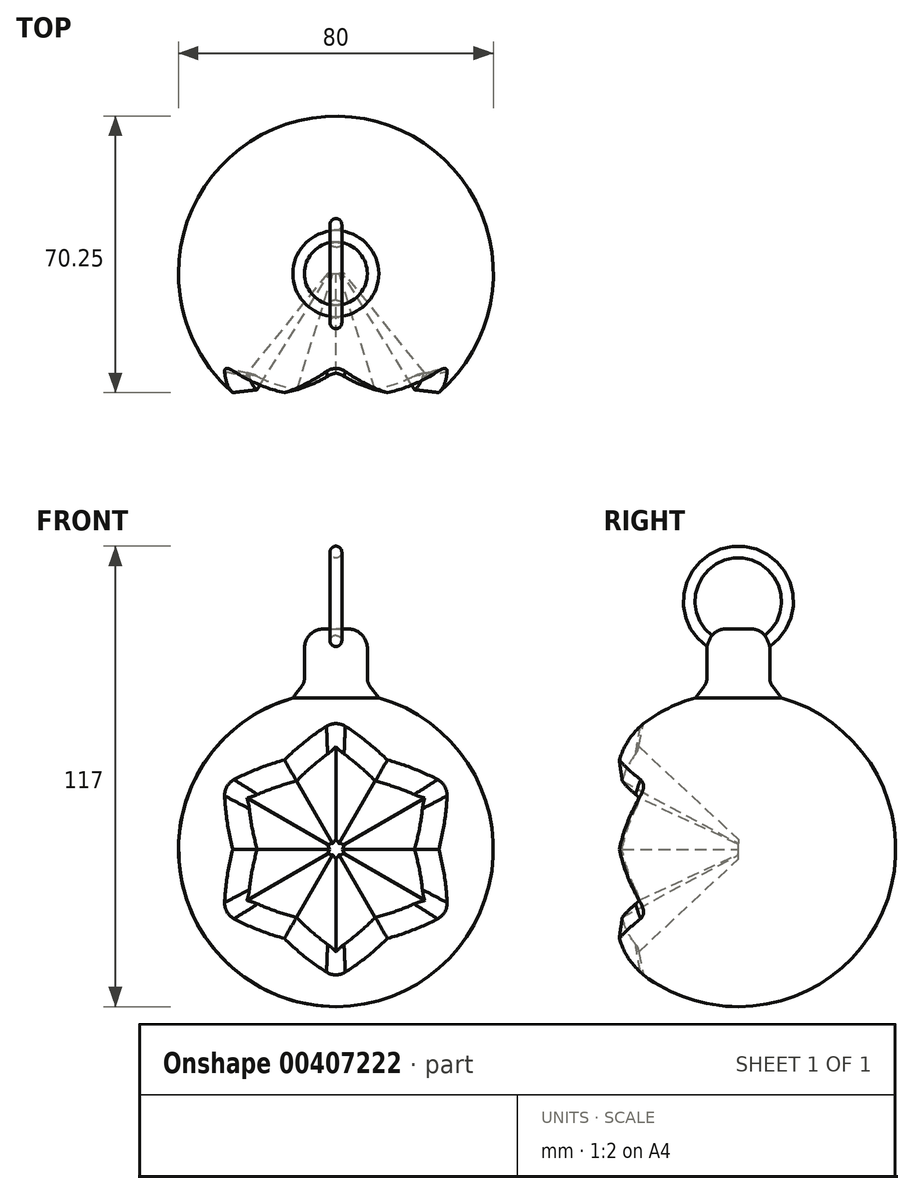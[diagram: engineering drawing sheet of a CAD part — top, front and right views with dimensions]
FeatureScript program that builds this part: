
annotation { "Feature Type Name" : "Feature", "Feature Type Description" : "" }
export const myFeature = defineFeature(function(context is Context, id is Id, definition is map)
    precondition{}
    {
        {
            var Q0;
            Q0=qCreatedBy(makeId("Front.planeOp"),FACE);
            var sketch = newSketch(context, id + "F0", { "sketchPlane" : qUnion([Q0])});
            skLineSegment(sketch, "E0", {"start": v(0, 40) * mm, "end": v(0, -40) * mm});
            skArc(sketch, "E1", {"start": v(0, 40) * mm, "mid": v(40, 0) * mm, "end": v(0, -40) * mm});
            skSolve(sketch);
        }
        {
            var Q0;
            Q0 = qSketchRegion(id + "F0", true);
            var Q1;
            Q1=sQuery(id+"F0.wireOp",EDGE,"E0");
            revolve(context, id + "F1", {"entities" : qUnion([Q0]), "axis" : qUnion([Q1]), "revolveType" : RevolveType.FULL});
        }
        {
            var Q0;
            Q0=qCreatedBy(makeId("Top.planeOp"),FACE);
            var sketch = newSketch(context, id + "F2", { "sketchPlane" : qUnion([Q0])});
            skCircle(sketch, "E2", {"center": v(0, 0) * mm, "radius": 8 * mm});
            skSolve(sketch);
        }
        {
            var Q0;
            Q0 = qSketchRegion(id + "F2", true);
            var Q1;
            Q1=sQuery(id+"F2.wireOp",EDGE,"E2");
            extrude(context, id + "F3", {"entities" : qUnion([Q0]), "operationType" : NewBodyOperationType.ADD, "surfaceEntities" : qUnion([Q1]), "depth" : 56 * mm});
        }
        {
            var Q0;
            Q0=qCreatedBy(makeId("Right.planeOp"),FACE);
            var sketch = newSketch(context, id + "F4", { "sketchPlane" : qUnion([Q0])});
            skCircle(sketch, "E3", {"center": v(0, 63) * mm, "radius": 11 * mm});
            skCircle(sketch, "E4.0", {"center": v(0, 63) * mm, "radius": 14 * mm});
            skSolve(sketch);
        }
        {
            var Q0;
            Q0 = qSketchRegion(id + "F4", true);
            extrude(context, id + "F5", {"entities" : qUnion([Q0]), "operationType" : NewBodyOperationType.ADD, "endBound" : BoundingType.SYMMETRIC, "depth" : 3 * mm});
        }
        {
            var Q0;
            Q0=makeQuery(id+"F5.opExtrude","CAP_EDGE",EDGE,{"disambiguationData":[OSD([sQuery(id+"F4.wireOp",EDGE,"E3")])],"isStart":true});
            var Q1;
            Q1=makeQuery(id+"F5.opExtrude","CAP_EDGE",EDGE,{"disambiguationData":[OSD([sQuery(id+"F4.wireOp",EDGE,"E4.0")])],"isStart":true});
            var Q2;
            Q2=makeQuery(id+"F5.opExtrude","CAP_EDGE",EDGE,{"disambiguationData":[OSD([sQuery(id+"F4.wireOp",EDGE,"E3")])],"isStart":false});
            var Q3;
            Q3=makeQuery(id+"F5.opExtrude","CAP_EDGE",EDGE,{"disambiguationData":[OSD([sQuery(id+"F4.wireOp",EDGE,"E4.0")])],"isStart":false});
            fillet(context, id + "F6", {"entities" : qUnion([Q0, Q1, Q2, Q3]), "radius" : 1.5 * mm, "tangentPropagation" : true, "allowEdgeOverflow" : false});
        }
        {
            var Q0;
            Q0=makeQuery(id+"F3.opExtrude","CAP_EDGE",EDGE,{"disambiguationData":[OSD([sQuery(id+"F2.wireOp",EDGE,"E2")])],"isStart":false});
            fillet(context, id + "F7", {"entities" : qUnion([Q0]), "radius" : 5 * mm, "tangentPropagation" : true, "allowEdgeOverflow" : false});
        }
        {
            var Q0;
            Q0=makeQuery(id+"F3.boolean.opBoolean","INTERSECT",EDGE,{"derivedFrom":[makeQuery(id+"F1.opRevolve","SWEPT_FACE",FACE,{"disambiguationData":[OSD([sQuery(id+"F0.wireOp",EDGE,"E1")])]}),makeQuery(id+"F3.opExtrude","SWEPT_FACE",FACE,{"disambiguationData":[OSD([sQuery(id+"F2.wireOp",EDGE,"E2")])]})]});
            chamfer(context, id + "F8", {"entities" : qUnion([Q0]), "width" : 4 * mm, "tangentPropagation" : true});
        }
        {
            var Q0;
            {var subQ0=makeQuery(id+"F3.opExtrude","SWEPT_FACE",FACE,{"disambiguationData":[OSD([sQuery(id+"F2.wireOp",EDGE,"E2")])]});Q0=makeQuery(id+"F8.opChamfer","BLEND_EDGE",EDGE,{"blendedFrom":[makeQuery(id+"F3.boolean.opBoolean","INTERSECT",EDGE,{"derivedFrom":[makeQuery(id+"F1.opRevolve","SWEPT_FACE",FACE,{"disambiguationData":[OSD([sQuery(id+"F0.wireOp",EDGE,"E1")])]}),subQ0]}),subQ0],"blendedInto":[subQ0]});}
            fillet(context, id + "F9", {"entities" : qUnion([Q0]), "radius" : 3 * mm, "tangentPropagation" : true, "allowEdgeOverflow" : false});
        }
        {
            var Q0;
            Q0=qCreatedBy(makeId("Front.planeOp"),FACE);
            var sketch = newSketch(context, id + "F10", { "sketchPlane" : qUnion([Q0])});
            skCircle(sketch, "E5.cCircle", {"center": v(0, 0) * mm, "radius": 2.5 * mm, "construction": true});
            skLineSegment(sketch, "E5.0", {"start": v(-2.17, 1.25) * mm, "end": v(0, 2.5) * mm, "construction": true});
            skLineSegment(sketch, "E5.1", {"start": v(0, 2.5) * mm, "end": v(2.17, 1.25) * mm, "construction": true});
            skLineSegment(sketch, "E5.2", {"start": v(2.17, 1.25) * mm, "end": v(2.17, -1.25) * mm, "construction": true});
            skLineSegment(sketch, "E5.3", {"start": v(2.17, -1.25) * mm, "end": v(0, -2.5) * mm, "construction": true});
            skLineSegment(sketch, "E5.4", {"start": v(0, -2.5) * mm, "end": v(-2.17, -1.25) * mm, "construction": true});
            skLineSegment(sketch, "E5.5", {"start": v(-2.17, -1.25) * mm, "end": v(-2.17, 1.25) * mm, "construction": true});
            skLineSegment(sketch, "E6", {"start": v(0, 2.5) * mm, "end": v(-0.83, 1.44) * mm});
            skLineSegment(sketch, "E7", {"start": v(-2.17, 1.25) * mm, "end": v(-0.83, 1.44) * mm});
            skLineSegment(sketch, "E8", {"start": v(-2.17, 1.25) * mm, "end": v(-1.67, 0) * mm});
            skLineSegment(sketch, "E9", {"start": v(-1.67, 0) * mm, "end": v(-2.17, -1.25) * mm});
            skLineSegment(sketch, "E10", {"start": v(-2.17, -1.25) * mm, "end": v(-0.83, -1.44) * mm});
            skLineSegment(sketch, "E11", {"start": v(-0.83, -1.44) * mm, "end": v(0, -2.5) * mm});
            skLineSegment(sketch, "E12", {"start": v(0, -2.5) * mm, "end": v(0.83, -1.44) * mm});
            skLineSegment(sketch, "E13", {"start": v(0.83, -1.44) * mm, "end": v(2.17, -1.25) * mm});
            skLineSegment(sketch, "E14", {"start": v(2.17, -1.25) * mm, "end": v(1.67, 0) * mm});
            skLineSegment(sketch, "E15", {"start": v(1.67, 0) * mm, "end": v(2.17, 1.25) * mm});
            skLineSegment(sketch, "E16", {"start": v(2.17, 1.25) * mm, "end": v(0.83, 1.44) * mm});
            skLineSegment(sketch, "E17", {"start": v(0.83, 1.44) * mm, "end": v(0, 2.5) * mm});
            skSolve(sketch);
        }
        {
            var Q0;
            Q0 = qSketchRegion(id + "F10", true);
            extrude(context, id + "F11", {"entities" : qUnion([Q0]), "operationType" : NewBodyOperationType.REMOVE, "depth" : 50 * mm, "hasDraft" : true, "draftAngle" : 30 * degree});
        }
        {
            var Q0;
            Q0=makeQuery(id+"F11.boolean.opBoolean","INTERSECT",EDGE,{"derivedFrom":[makeQuery(id+"F1.opRevolve","SWEPT_FACE",FACE,{"disambiguationData":[OSD([sQuery(id+"F0.wireOp",EDGE,"E1")])]}),makeQuery(id+"F11.opExtrude","SWEPT_FACE",FACE,{"disambiguationData":[OSD([sQuery(id+"F10.wireOp",EDGE,"E17")])]})]});
            var Q1;
            Q1=makeQuery(id+"F11.boolean.opBoolean","INTERSECT",EDGE,{"derivedFrom":[makeQuery(id+"F1.opRevolve","SWEPT_FACE",FACE,{"disambiguationData":[OSD([sQuery(id+"F0.wireOp",EDGE,"E1")])]}),makeQuery(id+"F11.opExtrude","SWEPT_FACE",FACE,{"disambiguationData":[OSD([sQuery(id+"F10.wireOp",EDGE,"E6")])]})]});
            var Q2;
            Q2=makeQuery(id+"F11.boolean.opBoolean","INTERSECT",EDGE,{"derivedFrom":[makeQuery(id+"F1.opRevolve","SWEPT_FACE",FACE,{"disambiguationData":[OSD([sQuery(id+"F0.wireOp",EDGE,"E1")])]}),makeQuery(id+"F11.opExtrude","SWEPT_FACE",FACE,{"disambiguationData":[OSD([sQuery(id+"F10.wireOp",EDGE,"E7")])]})]});
            var Q3;
            Q3=makeQuery(id+"F11.boolean.opBoolean","INTERSECT",EDGE,{"derivedFrom":[makeQuery(id+"F1.opRevolve","SWEPT_FACE",FACE,{"disambiguationData":[OSD([sQuery(id+"F0.wireOp",EDGE,"E1")])]}),makeQuery(id+"F11.opExtrude","SWEPT_FACE",FACE,{"disambiguationData":[OSD([sQuery(id+"F10.wireOp",EDGE,"E8")])]})]});
            var Q4;
            Q4=makeQuery(id+"F11.boolean.opBoolean","INTERSECT",EDGE,{"derivedFrom":[makeQuery(id+"F1.opRevolve","SWEPT_FACE",FACE,{"disambiguationData":[OSD([sQuery(id+"F0.wireOp",EDGE,"E1")])]}),makeQuery(id+"F11.opExtrude","SWEPT_FACE",FACE,{"disambiguationData":[OSD([sQuery(id+"F10.wireOp",EDGE,"E9")])]})]});
            var Q5;
            Q5=makeQuery(id+"F11.boolean.opBoolean","INTERSECT",EDGE,{"derivedFrom":[makeQuery(id+"F1.opRevolve","SWEPT_FACE",FACE,{"disambiguationData":[OSD([sQuery(id+"F0.wireOp",EDGE,"E1")])]}),makeQuery(id+"F11.opExtrude","SWEPT_FACE",FACE,{"disambiguationData":[OSD([sQuery(id+"F10.wireOp",EDGE,"E10")])]})]});
            var Q6;
            Q6=makeQuery(id+"F11.boolean.opBoolean","INTERSECT",EDGE,{"derivedFrom":[makeQuery(id+"F1.opRevolve","SWEPT_FACE",FACE,{"disambiguationData":[OSD([sQuery(id+"F0.wireOp",EDGE,"E1")])]}),makeQuery(id+"F11.opExtrude","SWEPT_FACE",FACE,{"disambiguationData":[OSD([sQuery(id+"F10.wireOp",EDGE,"E11")])]})]});
            var Q7;
            Q7=makeQuery(id+"F11.boolean.opBoolean","INTERSECT",EDGE,{"derivedFrom":[makeQuery(id+"F1.opRevolve","SWEPT_FACE",FACE,{"disambiguationData":[OSD([sQuery(id+"F0.wireOp",EDGE,"E1")])]}),makeQuery(id+"F11.opExtrude","SWEPT_FACE",FACE,{"disambiguationData":[OSD([sQuery(id+"F10.wireOp",EDGE,"E12")])]})]});
            var Q8;
            Q8=makeQuery(id+"F11.boolean.opBoolean","INTERSECT",EDGE,{"derivedFrom":[makeQuery(id+"F1.opRevolve","SWEPT_FACE",FACE,{"disambiguationData":[OSD([sQuery(id+"F0.wireOp",EDGE,"E1")])]}),makeQuery(id+"F11.opExtrude","SWEPT_FACE",FACE,{"disambiguationData":[OSD([sQuery(id+"F10.wireOp",EDGE,"E13")])]})]});
            var Q9;
            Q9=makeQuery(id+"F11.boolean.opBoolean","INTERSECT",EDGE,{"derivedFrom":[makeQuery(id+"F1.opRevolve","SWEPT_FACE",FACE,{"disambiguationData":[OSD([sQuery(id+"F0.wireOp",EDGE,"E1")])]}),makeQuery(id+"F11.opExtrude","SWEPT_FACE",FACE,{"disambiguationData":[OSD([sQuery(id+"F10.wireOp",EDGE,"E14")])]})]});
            var Q10;
            Q10=makeQuery(id+"F11.boolean.opBoolean","INTERSECT",EDGE,{"derivedFrom":[makeQuery(id+"F1.opRevolve","SWEPT_FACE",FACE,{"disambiguationData":[OSD([sQuery(id+"F0.wireOp",EDGE,"E1")])]}),makeQuery(id+"F11.opExtrude","SWEPT_FACE",FACE,{"disambiguationData":[OSD([sQuery(id+"F10.wireOp",EDGE,"E15")])]})]});
            var Q11;
            Q11=makeQuery(id+"F11.boolean.opBoolean","INTERSECT",EDGE,{"derivedFrom":[makeQuery(id+"F1.opRevolve","SWEPT_FACE",FACE,{"disambiguationData":[OSD([sQuery(id+"F0.wireOp",EDGE,"E1")])]}),makeQuery(id+"F11.opExtrude","SWEPT_FACE",FACE,{"disambiguationData":[OSD([sQuery(id+"F10.wireOp",EDGE,"E16")])]})]});
            chamfer(context, id + "F12", {"entities" : qUnion([Q0, Q1, Q2, Q3, Q4, Q5, Q6, Q7, Q8, Q9, Q10, Q11]), "width" : 4 * mm, "tangentPropagation" : true});
        }
        {
            var Q0;
            {var subQ0=makeQuery(id+"F1.opRevolve","SWEPT_FACE",FACE,{"disambiguationData":[OSD([sQuery(id+"F0.wireOp",EDGE,"E1")])]});Q0=makeQuery(id+"F12.opChamfer","BLEND_EDGE",EDGE,{"blendedFrom":[makeQuery(id+"F11.boolean.opBoolean","INTERSECT",EDGE,{"derivedFrom":[subQ0,makeQuery(id+"F11.opExtrude","SWEPT_FACE",FACE,{"disambiguationData":[OSD([sQuery(id+"F10.wireOp",EDGE,"E6")])]})]}),makeQuery(id+"F11.boolean.opBoolean","INTERSECT",EDGE,{"derivedFrom":[subQ0,makeQuery(id+"F11.opExtrude","SWEPT_FACE",FACE,{"disambiguationData":[OSD([sQuery(id+"F10.wireOp",EDGE,"E17")])]})]})],"blendedInto":[]});}
            var Q1;
            {var subQ0=makeQuery(id+"F1.opRevolve","SWEPT_FACE",FACE,{"disambiguationData":[OSD([sQuery(id+"F0.wireOp",EDGE,"E1")])]});Q1=makeQuery(id+"F12.opChamfer","BLEND_EDGE",EDGE,{"blendedFrom":[makeQuery(id+"F11.boolean.opBoolean","INTERSECT",EDGE,{"derivedFrom":[subQ0,makeQuery(id+"F11.opExtrude","SWEPT_FACE",FACE,{"disambiguationData":[OSD([sQuery(id+"F10.wireOp",EDGE,"E7")])]})]}),makeQuery(id+"F11.boolean.opBoolean","INTERSECT",EDGE,{"derivedFrom":[subQ0,makeQuery(id+"F11.opExtrude","SWEPT_FACE",FACE,{"disambiguationData":[OSD([sQuery(id+"F10.wireOp",EDGE,"E8")])]})]})],"blendedInto":[]});}
            var Q2;
            {var subQ0=makeQuery(id+"F1.opRevolve","SWEPT_FACE",FACE,{"disambiguationData":[OSD([sQuery(id+"F0.wireOp",EDGE,"E1")])]});Q2=makeQuery(id+"F12.opChamfer","BLEND_EDGE",EDGE,{"blendedFrom":[makeQuery(id+"F11.boolean.opBoolean","INTERSECT",EDGE,{"derivedFrom":[subQ0,makeQuery(id+"F11.opExtrude","SWEPT_FACE",FACE,{"disambiguationData":[OSD([sQuery(id+"F10.wireOp",EDGE,"E9")])]})]}),makeQuery(id+"F11.boolean.opBoolean","INTERSECT",EDGE,{"derivedFrom":[subQ0,makeQuery(id+"F11.opExtrude","SWEPT_FACE",FACE,{"disambiguationData":[OSD([sQuery(id+"F10.wireOp",EDGE,"E10")])]})]})],"blendedInto":[]});}
            var Q3;
            {var subQ0=makeQuery(id+"F1.opRevolve","SWEPT_FACE",FACE,{"disambiguationData":[OSD([sQuery(id+"F0.wireOp",EDGE,"E1")])]});Q3=makeQuery(id+"F12.opChamfer","BLEND_EDGE",EDGE,{"blendedFrom":[makeQuery(id+"F11.boolean.opBoolean","INTERSECT",EDGE,{"derivedFrom":[subQ0,makeQuery(id+"F11.opExtrude","SWEPT_FACE",FACE,{"disambiguationData":[OSD([sQuery(id+"F10.wireOp",EDGE,"E11")])]})]}),makeQuery(id+"F11.boolean.opBoolean","INTERSECT",EDGE,{"derivedFrom":[subQ0,makeQuery(id+"F11.opExtrude","SWEPT_FACE",FACE,{"disambiguationData":[OSD([sQuery(id+"F10.wireOp",EDGE,"E12")])]})]})],"blendedInto":[]});}
            var Q4;
            {var subQ0=makeQuery(id+"F1.opRevolve","SWEPT_FACE",FACE,{"disambiguationData":[OSD([sQuery(id+"F0.wireOp",EDGE,"E1")])]});Q4=makeQuery(id+"F12.opChamfer","BLEND_EDGE",EDGE,{"blendedFrom":[makeQuery(id+"F11.boolean.opBoolean","INTERSECT",EDGE,{"derivedFrom":[subQ0,makeQuery(id+"F11.opExtrude","SWEPT_FACE",FACE,{"disambiguationData":[OSD([sQuery(id+"F10.wireOp",EDGE,"E13")])]})]}),makeQuery(id+"F11.boolean.opBoolean","INTERSECT",EDGE,{"derivedFrom":[subQ0,makeQuery(id+"F11.opExtrude","SWEPT_FACE",FACE,{"disambiguationData":[OSD([sQuery(id+"F10.wireOp",EDGE,"E14")])]})]})],"blendedInto":[]});}
            var Q5;
            {var subQ0=makeQuery(id+"F1.opRevolve","SWEPT_FACE",FACE,{"disambiguationData":[OSD([sQuery(id+"F0.wireOp",EDGE,"E1")])]});Q5=makeQuery(id+"F12.opChamfer","BLEND_EDGE",EDGE,{"blendedFrom":[makeQuery(id+"F11.boolean.opBoolean","INTERSECT",EDGE,{"derivedFrom":[subQ0,makeQuery(id+"F11.opExtrude","SWEPT_FACE",FACE,{"disambiguationData":[OSD([sQuery(id+"F10.wireOp",EDGE,"E15")])]})]}),makeQuery(id+"F11.boolean.opBoolean","INTERSECT",EDGE,{"derivedFrom":[subQ0,makeQuery(id+"F11.opExtrude","SWEPT_FACE",FACE,{"disambiguationData":[OSD([sQuery(id+"F10.wireOp",EDGE,"E16")])]})]})],"blendedInto":[]});}
            fillet(context, id + "F13", {"entities" : qUnion([Q0, Q1, Q2, Q3, Q4, Q5]), "radius" : 5 * mm, "tangentPropagation" : true, "allowEdgeOverflow" : false});
        }
    });
